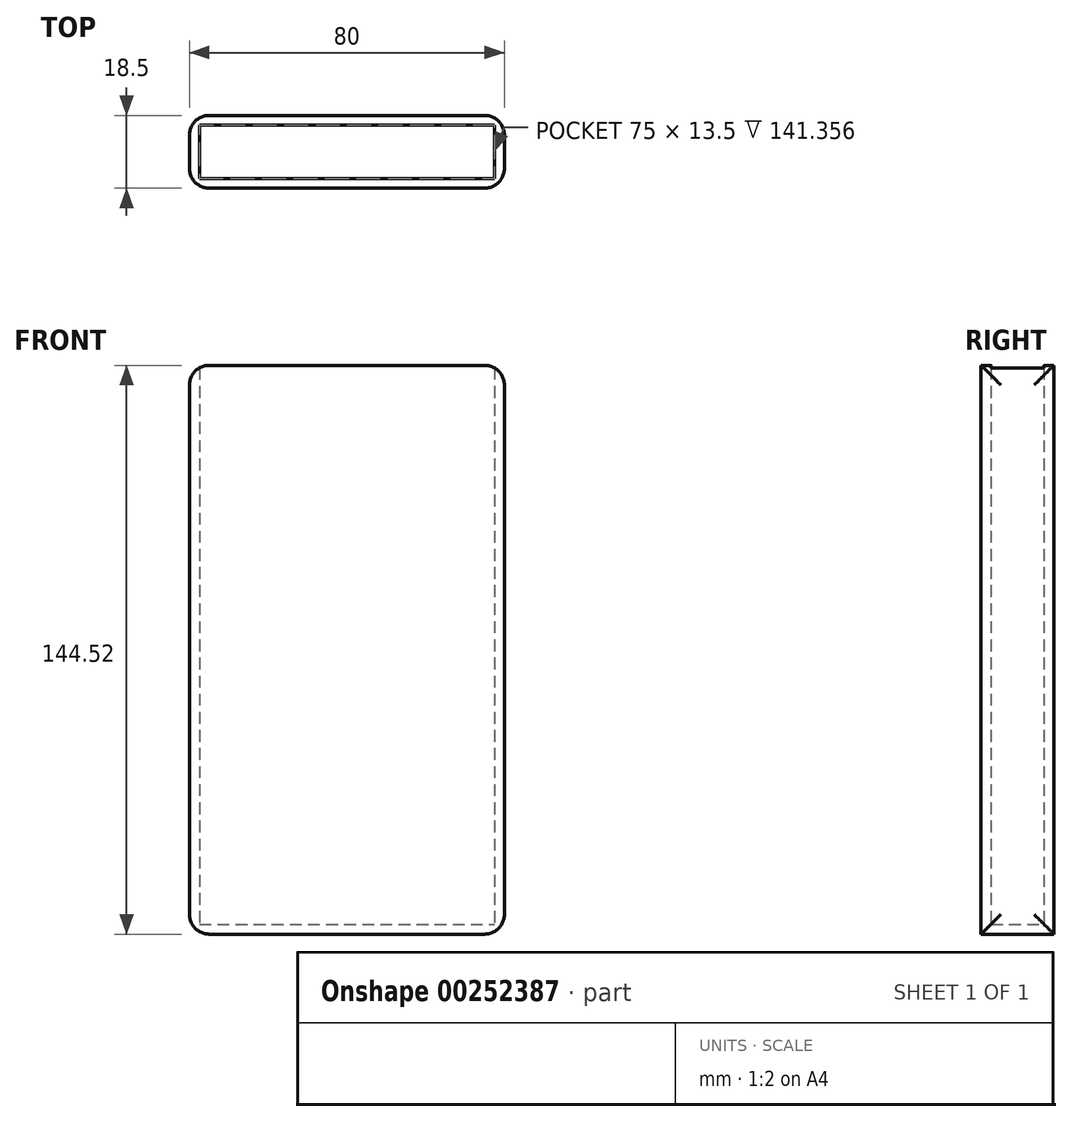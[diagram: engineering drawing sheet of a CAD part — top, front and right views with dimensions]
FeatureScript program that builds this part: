
annotation { "Feature Type Name" : "Feature", "Feature Type Description" : "" }
export const myFeature = defineFeature(function(context is Context, id is Id, definition is map)
    precondition{}
    {
        {
            var Q0;
            Q0=qCreatedBy(makeId("Front.planeOp"),FACE);
            var sketch = newSketch(context, id + "F0", { "sketchPlane" : qUnion([Q0])});
            skLineSegment(sketch, "E0.bottom", {"start": v(-35.48, 75.41) * mm, "end": v(44.52, 75.41) * mm});
            skLineSegment(sketch, "E0.top", {"start": v(-35.48, -69.11) * mm, "end": v(44.52, -69.11) * mm});
            skLineSegment(sketch, "E0.left", {"start": v(-35.48, 75.41) * mm, "end": v(-35.48, -69.11) * mm});
            skLineSegment(sketch, "E0.right", {"start": v(44.52, 75.41) * mm, "end": v(44.52, -69.11) * mm});
            skSolve(sketch);
        }
        {
            var Q0;
            Q0=makeQuery(id+"F0.imprint","IMPRINT",FACE,{"disambiguationData":[TD([[makeQuery(id+"F0.imprint","IMPRINT",EDGE,{"derivedFrom":sQuery(id+"F0.wireOp",EDGE,"E0.bottom")}),-1.0]])]});
            extrude(context, id + "F1", {"entities" : qUnion([Q0]), "depth" : 18.5 * mm});
        }
        {
            var Q0;
            Q0=makeQuery(id+"F1.opExtrude","SWEPT_FACE",FACE,{"disambiguationData":[OSD([sQuery(id+"F0.wireOp",EDGE,"E0.bottom")])]});
            shell(context, id + "F2", {"entities" : qUnion([Q0]), "thickness" : 2.5 * mm});
        }
        {
            var Q0;
            Q0=makeQuery(id+"F1.opExtrude","CAP_EDGE",EDGE,{"disambiguationData":[OSD([sQuery(id+"F0.wireOp",EDGE,"E0.left")])],"isStart":false});
            var Q1;
            Q1=makeQuery(id+"F1.opExtrude","CAP_EDGE",EDGE,{"disambiguationData":[OSD([sQuery(id+"F0.wireOp",EDGE,"E0.left")])],"isStart":true});
            var Q2;
            Q2=makeQuery(id+"F1.opExtrude","CAP_EDGE",EDGE,{"disambiguationData":[OSD([sQuery(id+"F0.wireOp",EDGE,"E0.right")])],"isStart":false});
            var Q3;
            Q3=makeQuery(id+"F1.opExtrude","CAP_EDGE",EDGE,{"disambiguationData":[OSD([sQuery(id+"F0.wireOp",EDGE,"E0.right")])],"isStart":true});
            var Q4;
            Q4=makeQuery(id+"F1.opExtrude","SWEPT_EDGE",EDGE,{"disambiguationData":[OSD([sQuery(id+"F0.wireOp",EDGE,"E0.bottom"),sQuery(id+"F0.wireOp",EDGE,"E0.right")])]});
            var Q5;
            Q5=makeQuery(id+"F1.opExtrude","SWEPT_EDGE",EDGE,{"disambiguationData":[OSD([sQuery(id+"F0.wireOp",EDGE,"E0.bottom"),sQuery(id+"F0.wireOp",EDGE,"E0.left")])]});
            var Q6;
            Q6=makeQuery(id+"F1.opExtrude","SWEPT_EDGE",EDGE,{"disambiguationData":[OSD([sQuery(id+"F0.wireOp",EDGE,"E0.top"),sQuery(id+"F0.wireOp",EDGE,"E0.left")])]});
            var Q7;
            Q7=makeQuery(id+"F1.opExtrude","SWEPT_EDGE",EDGE,{"disambiguationData":[OSD([sQuery(id+"F0.wireOp",EDGE,"E0.top"),sQuery(id+"F0.wireOp",EDGE,"E0.right")])]});
            fillet(context, id + "F3", {"entities" : qUnion([Q0, Q1, Q2, Q3, Q4, Q5, Q6, Q7]), "radius" : 5 * mm, "tangentPropagation" : true, "allowEdgeOverflow" : false});
        }
    });
